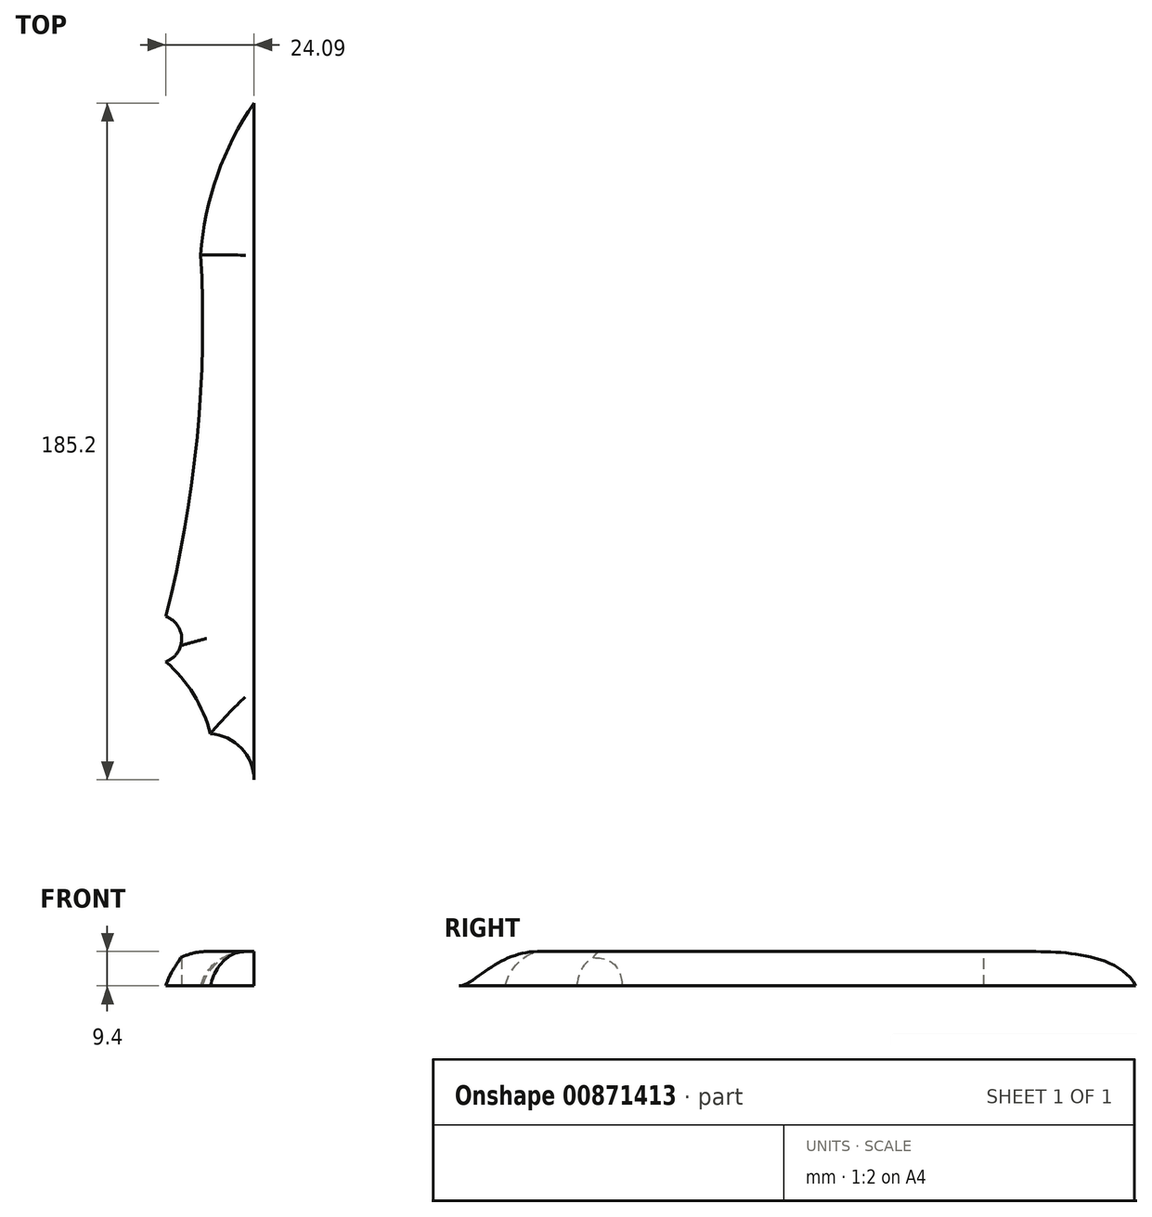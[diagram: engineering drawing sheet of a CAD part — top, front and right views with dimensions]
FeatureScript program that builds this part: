
annotation { "Feature Type Name" : "Feature", "Feature Type Description" : "" }
export const myFeature = defineFeature(function(context is Context, id is Id, definition is map)
    precondition{}
    {
        {
            var Q0;
            Q0=qCreatedBy(makeId("Top.planeOp"),FACE);
            var sketch = newSketch(context, id + "F0", { "sketchPlane" : qUnion([Q0])});
            skLineSegment(sketch, "E0", {"start": v(0, -95.7) * mm, "end": v(0, 89.5) * mm});
            skArc(sketch, "E1", {"start": v(0, 89.5) * mm, "mid": v(-10.05, 69.73) * mm, "end": v(-14.56, 48.02) * mm});
            skArc(sketch, "E2", {"start": v(-24.1, -51) * mm, "mid": v(-15.54, -1.86) * mm, "end": v(-14.56, 48.02) * mm});
            skArc(sketch, "E3", {"start": v(-24.1, -63.36) * mm, "mid": v(-19.77, -57.18) * mm, "end": v(-24.1, -51) * mm});
            skArc(sketch, "E4", {"start": v(-11.9, -83.1) * mm, "mid": v(-16.52, -72.32) * mm, "end": v(-24.1, -63.36) * mm});
            skArc(sketch, "E5", {"start": v(0, -95.7) * mm, "mid": v(-3.45, -87.03) * mm, "end": v(-11.9, -83.1) * mm});
            skSolve(sketch);
        }
        {
            var Q0;
            Q0=makeQuery(id+"F0.imprint","IMPRINT",FACE,{"disambiguationData":[TD([[makeQuery(id+"F0.imprint","IMPRINT",EDGE,{"derivedFrom":sQuery(id+"F0.wireOp",EDGE,"E0")}),1.0]])]});
            extrude(context, id + "F1", {"entities" : qUnion([Q0]), "depth" : 9.4 * mm, "offsetDistance" : 25.4 * mm});
        }
        {
            var Q0;
            Q0=makeQuery(id+"F1.opExtrude","CAP_EDGE",EDGE,{"disambiguationData":[OSD([sQuery(id+"F0.wireOp",EDGE,"E1")])],"isStart":false});
            var Q1;
            Q1=makeQuery(id+"F1.opExtrude","CAP_EDGE",EDGE,{"disambiguationData":[OSD([sQuery(id+"F0.wireOp",EDGE,"E2")])],"isStart":false});
            var Q2;
            Q2=makeQuery(id+"F1.opExtrude","CAP_EDGE",EDGE,{"disambiguationData":[OSD([sQuery(id+"F0.wireOp",EDGE,"E4")])],"isStart":false});
            var Q3;
            Q3=makeQuery(id+"F1.opExtrude","CAP_EDGE",EDGE,{"disambiguationData":[OSD([sQuery(id+"F0.wireOp",EDGE,"E5")])],"isStart":false});
            fillet(context, id + "F2", {"entities" : qUnion([Q0, Q1, Q2, Q3]), "radius" : 12.7 * mm, "tangentPropagation" : true, "allowEdgeOverflow" : false});
        }
    });
